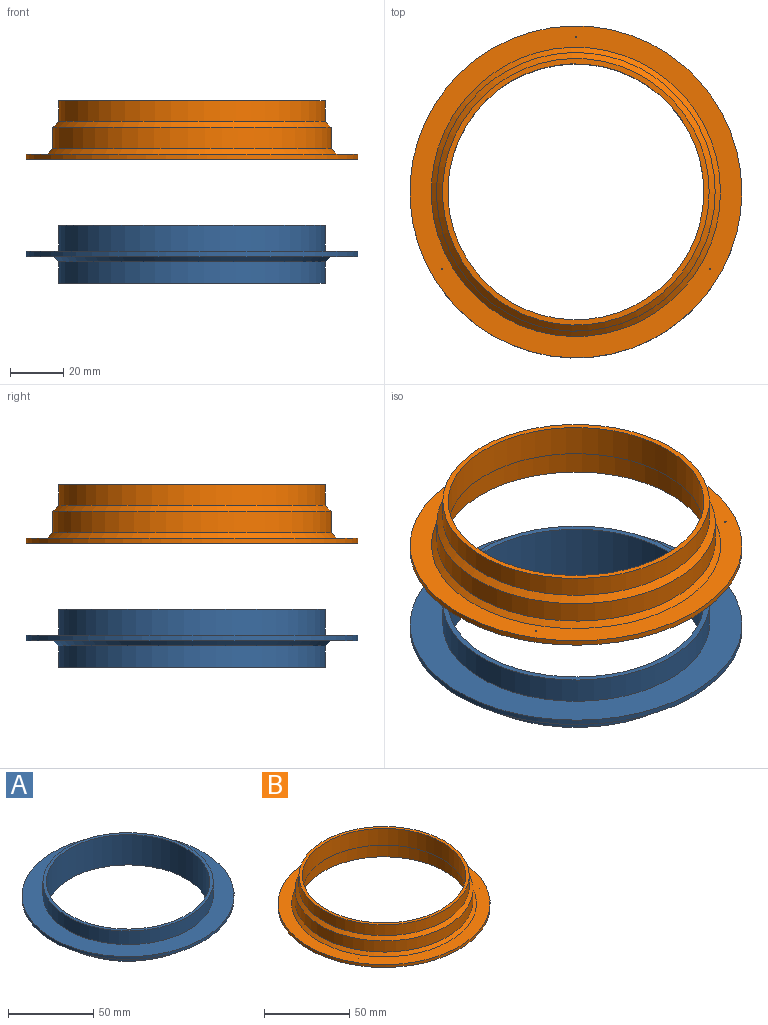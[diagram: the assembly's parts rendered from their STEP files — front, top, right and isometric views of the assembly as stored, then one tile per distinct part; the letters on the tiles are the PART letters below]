
ASSEMBLY  parts=2 mates=1
PART A: 15 faces, bbox 124.5x124.5x21.8 mm
  f0: cylinder r=50mm len=100mm, axis (0,0,1), area 2513.3mm2, adj f1,f8
  f1: plane 100x100mm, normal (0,0,-1), area 615.8mm2, adj f0,f2
  f2: cylinder r=48mm len=96mm, axis (0,0,1), area 6559.6mm2, adj f1,f3
  f3: plane 100x100mm, normal (0,0,1), area 615.8mm2, adj f2,f4
  f4: cylinder r=50mm len=100mm, axis (0,0,1), area 3063.1mm2, adj f3,f5
  f5: plane 124.5x124.5mm, normal (0,0,1), area 4319.9mm2, adj f4,f6
  f6: cylinder r=62.25mm len=124.5mm, axis (0,0,1), area 782.3mm2, adj f5,f7
  f7: plane 124.5x124.5mm, normal (0,0,-1), area 3678.4mm2, adj f6,f8,f10,f12,f14
  f8: cone r=52mm half-angle=45deg, axis (0,0,1), area 906.3mm2, adj f0,f7
  f9: cone r=0mm half-angle=59deg, axis (0,0,-1), area 0.2mm2, adj f10
  f10: cylinder r=0.25mm len=0.5mm, axis (0,0,-1), area 0.8mm2, adj f7,f9
  f11: cone r=0mm half-angle=59deg, axis (0,0,-1), area 0.2mm2, adj f12
  f12: cylinder r=0.25mm len=0.5mm, axis (0,0,-1), area 0.8mm2, adj f7,f11
  f13: cone r=0mm half-angle=59deg, axis (0,0,-1), area 0.2mm2, adj f14
  f14: cylinder r=0.25mm len=0.5mm, axis (0,0,-1), area 0.8mm2, adj f7,f13
PART B: 17 faces, bbox 124.5x124.5x22 mm
  f0: plane 124.5x124.5mm, normal (0,0,-1), area 4241.2mm2, adj f1,f10
  f1: cylinder r=50.25mm len=100.5mm, axis (0,0,1), area 3157.3mm2, adj f0,f2
  f2: plane 100.5x100.5mm, normal (0,0,-1), area 694.5mm2, adj f1,f3
  f3: cylinder r=48mm len=96mm, axis (0,0,1), area 3619.1mm2, adj f2,f4
  f4: plane 100x100mm, normal (0,0,1), area 615.8mm2, adj f3,f5
  f5: cylinder r=50mm len=100mm, axis (0,0,1), area 2434.7mm2, adj f4,f6
  f6: cone r=52.25mm half-angle=45deg, axis (0,0,-1), area 1022.1mm2, adj f5,f7
  f7: cylinder r=52.25mm len=104.5mm, axis (0,0,1), area 2626.4mm2, adj f6,f8
  f8: cone r=54.25mm half-angle=45deg, axis (0,0,-1), area 946.3mm2, adj f7,f9
  f9: plane 124.5x124.5mm, normal (0,0,1), area 2927.4mm2, adj f8,f10,f12,f14,f16
  f10: cylinder r=62.25mm len=124.5mm, axis (0,0,1), area 782.3mm2, adj f0,f9
  f11: cone r=0mm half-angle=59deg, axis (0,0,1), area 0.2mm2, adj f12
  f12: cylinder r=0.25mm len=0.5mm, axis (0,0,1), area 0.8mm2, adj f9,f11
  f13: cone r=0mm half-angle=59deg, axis (0,0,1), area 0.2mm2, adj f14
  f14: cylinder r=0.25mm len=0.5mm, axis (0,0,1), area 0.8mm2, adj f9,f13
  f15: cone r=0mm half-angle=59deg, axis (0,0,1), area 0.2mm2, adj f16
  f16: cylinder r=0.25mm len=0.5mm, axis (0,0,1), area 0.8mm2, adj f9,f15
PLACE A t=(-69.28,-37.35,-44.13)mm
PLACE B t=(-69.28,-37.35,-8.39)mm
MATE cylindrical B.f1 <-> A.f8  axis (0,0,1) through (-69.28,-37.35,-3.39)mm
